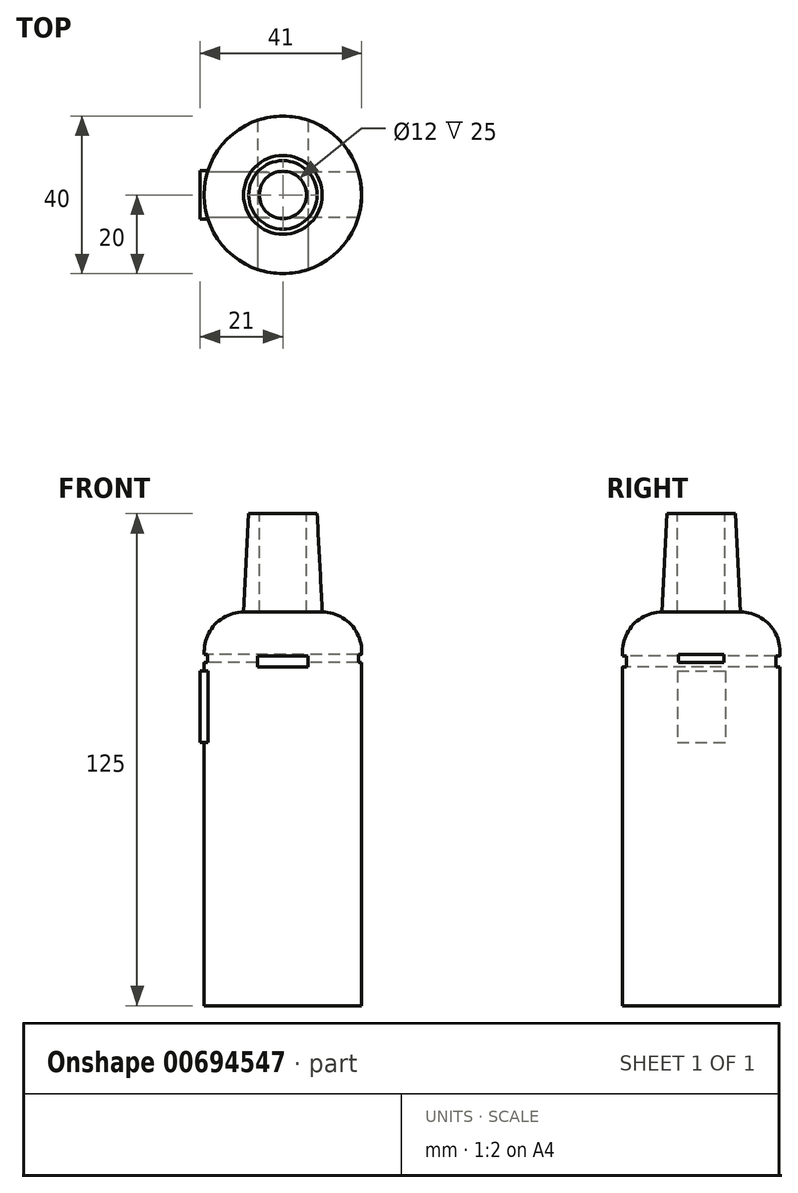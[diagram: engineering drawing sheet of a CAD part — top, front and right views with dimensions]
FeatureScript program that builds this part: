
annotation { "Feature Type Name" : "Feature", "Feature Type Description" : "" }
export const myFeature = defineFeature(function(context is Context, id is Id, definition is map)
    precondition{}
    {
        {
            var Q0;
            Q0=qCreatedBy(makeId("Top.planeOp"),FACE);
            var sketch = newSketch(context, id + "F0", { "sketchPlane" : qUnion([Q0])});
            skCircle(sketch, "E0", {"center": v(0, 0) * mm, "radius": 20 * mm});
            skSolve(sketch);
        }
        {
            var Q0;
            Q0=makeQuery(id+"F0.imprint","IMPRINT",FACE,{"disambiguationData":[TD([[makeQuery(id+"F0.imprint","IMPRINT",EDGE,{"derivedFrom":sQuery(id+"F0.wireOp",EDGE,"E0")}),1.0]])]});
            extrude(context, id + "F1", {"entities" : qUnion([Q0]), "depth" : 100 * mm, "offsetDistance" : 25 * mm});
        }
        {
            var Q0;
            Q0=makeQuery(id+"F1.opExtrude","CAP_FACE",FACE,{"disambiguationData":[OSD([sQuery(id+"F0.wireOp",EDGE,"E0")])],"isStart":false});
            var sketch = newSketch(context, id + "F2", { "sketchPlane" : qUnion([Q0])});
            skCircle(sketch, "E1", {"center": v(0, 0) * mm, "radius": 10 * mm});
            skSolve(sketch);
        }
        {
            var Q0;
            Q0=makeQuery(id+"F2.imprint","IMPRINT",FACE,{"disambiguationData":[TD([[makeQuery(id+"F2.imprint","IMPRINT",EDGE,{"derivedFrom":sQuery(id+"F2.wireOp",EDGE,"E1")}),1.0]])]});
            var Q1;
            Q1=sQuery(id+"F2.wireOp",EDGE,"E1");
            extrude(context, id + "F3", {"entities" : qUnion([Q0]), "surfaceEntities" : qUnion([Q1]), "depth" : 25 * mm, "offsetDistance" : 25 * mm, "hasDraft" : true, "draftAngle" : 3 * degree, "draftPullDirection" : true});
        }
        {
            var Q0;
            Q0=makeQuery(id+"F1.opExtrude","CAP_FACE",FACE,{"disambiguationData":[OSD([sQuery(id+"F0.wireOp",EDGE,"E0")])],"isStart":false});
            fillet(context, id + "F4", {"entities" : qUnion([Q0]), "radius" : 10 * mm, "tangentPropagation" : true, "allowEdgeOverflow" : false});
        }
        {
            var Q0;
            Q0=makeQuery(id+"F3.opExtrude","CAP_FACE",FACE,{"disambiguationData":[OSD([sQuery(id+"F2.wireOp",EDGE,"E1")])],"isStart":false});
            var sketch = newSketch(context, id + "F5", { "sketchPlane" : qUnion([Q0])});
            skCircle(sketch, "E2", {"center": v(0, 0) * mm, "radius": 6 * mm});
            skSolve(sketch);
        }
        {
            var Q0;
            Q0=makeQuery(id+"F5.imprint","IMPRINT",FACE,{"disambiguationData":[TD([[makeQuery(id+"F5.imprint","IMPRINT",EDGE,{"derivedFrom":sQuery(id+"F5.wireOp",EDGE,"E2")}),1.0]])]});
            var Q1;
            Q1=sQuery(id+"F5.wireOp",EDGE,"E2");
            extrude(context, id + "F6", {"entities" : qUnion([Q0]), "operationType" : NewBodyOperationType.REMOVE, "surfaceEntities" : qUnion([Q1]), "oppositeDirection" : true, "depth" : 25 * mm, "offsetDistance" : 25 * mm});
        }
        {
            var Q0;
            Q0=qCreatedBy(makeId("Right.planeOp"),FACE);
            cPlane(context, id + "F7", {"entities" : qUnion([Q0]), "cplaneType" : CPlaneType.OFFSET, "offset" : 18 * mm, "oppositeDirection" : true, "width" : 150 * mm, "height" : 150 * mm});
        }
        {
            var Q0;
            Q0=qCreatedBy(id+"F7.planeOp",FACE);
            var sketch = newSketch(context, id + "F8", { "sketchPlane" : qUnion([Q0])});
            skLineSegment(sketch, "E3.bottom", {"start": v(-6.11, 66.93) * mm, "end": v(6.11, 66.93) * mm});
            skLineSegment(sketch, "E3.top", {"start": v(-6.11, 85.1) * mm, "end": v(6.11, 85.1) * mm});
            skLineSegment(sketch, "E3.left", {"start": v(-6.11, 66.93) * mm, "end": v(-6.11, 85.1) * mm});
            skLineSegment(sketch, "E3.right", {"start": v(6.11, 66.93) * mm, "end": v(6.11, 85.1) * mm});
            skPoint(sketch, "E3.middle", {"position": v(0, 76.01) * mm});
            skSolve(sketch);
        }
        {
            var Q0;
            Q0 = qSketchRegion(id + "F8", true);
            extrude(context, id + "F9", {"entities" : qUnion([Q0]), "operationType" : NewBodyOperationType.ADD, "oppositeDirection" : true, "depth" : 3 * mm, "offsetDistance" : 25 * mm});
        }
        {
            var Q0;
            Q0=qCreatedBy(makeId("Front.planeOp"),FACE);
            cPlane(context, id + "F10", {"entities" : qUnion([Q0]), "cplaneType" : CPlaneType.OFFSET, "offset" : 21 * mm, "width" : 150 * mm, "height" : 150 * mm});
        }
        {
            var Q0;
            Q0=qCreatedBy(id+"F10.planeOp",FACE);
            var sketch = newSketch(context, id + "F11", { "sketchPlane" : qUnion([Q0])});
            skLineSegment(sketch, "E4.bottom", {"start": v(6.4, 86.1) * mm, "end": v(-6.4, 86.1) * mm});
            skLineSegment(sketch, "E4.top", {"start": v(6.4, 88.9) * mm, "end": v(-6.4, 88.9) * mm});
            skLineSegment(sketch, "E4.left", {"start": v(6.4, 86.1) * mm, "end": v(6.4, 88.9) * mm});
            skLineSegment(sketch, "E4.right", {"start": v(-6.4, 86.1) * mm, "end": v(-6.4, 88.9) * mm});
            skPoint(sketch, "E4.middle", {"position": v(0, 87.5) * mm});
            skSolve(sketch);
        }
        {
            var Q0;
            Q0 = qSketchRegion(id + "F11", true);
            extrude(context, id + "F12", {"entities" : qUnion([Q0]), "operationType" : NewBodyOperationType.REMOVE, "oppositeDirection" : true, "depth" : 50 * mm, "offsetDistance" : 25 * mm});
        }
        {
            var Q0;
            Q0=qCreatedBy(makeId("Right.planeOp"),FACE);
            cPlane(context, id + "F13", {"entities" : qUnion([Q0]), "cplaneType" : CPlaneType.OFFSET, "offset" : 21 * mm, "oppositeDirection" : true, "width" : 150 * mm, "height" : 150 * mm});
        }
        {
            var Q0;
            Q0=qCreatedBy(id+"F13.planeOp",FACE);
            var sketch = newSketch(context, id + "F14", { "sketchPlane" : qUnion([Q0])});
            skLineSegment(sketch, "E5.bottom", {"start": v(-5.77, 87.15) * mm, "end": v(5.77, 87.15) * mm});
            skLineSegment(sketch, "E5.top", {"start": v(-5.77, 89.25) * mm, "end": v(5.77, 89.25) * mm});
            skLineSegment(sketch, "E5.left", {"start": v(-5.77, 87.15) * mm, "end": v(-5.77, 89.25) * mm});
            skLineSegment(sketch, "E5.right", {"start": v(5.77, 87.15) * mm, "end": v(5.77, 89.25) * mm});
            skPoint(sketch, "E5.middle", {"position": v(0, 88.2) * mm});
            skSolve(sketch);
        }
        {
            var Q0;
            Q0 = qSketchRegion(id + "F14", true);
            extrude(context, id + "F15", {"entities" : qUnion([Q0]), "operationType" : NewBodyOperationType.REMOVE, "depth" : 50 * mm, "offsetDistance" : 25 * mm});
        }
    });
